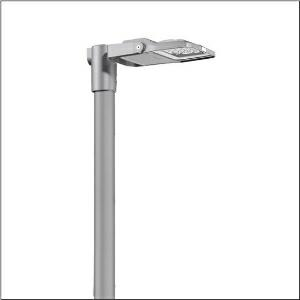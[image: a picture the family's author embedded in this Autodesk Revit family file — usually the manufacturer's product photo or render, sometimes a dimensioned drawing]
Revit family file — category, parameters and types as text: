
# Revit family: floodlight_fl_21_micro___pl33t_5xa7761a2f3a_8016
name_source: partatom
category: Lighting Fixtures
units: mm (PartAtom-declared; Revit-internal decimal feet)

## family parameters
Cut with Voids When Loaded = No
Host = Face
Light Source = No
Part Type = Normal
Room Calculation Point = No
Round Connector Dimension = Use Diameter
Shared = No

## types (1)
- --- (1 x LED, 2930 lm, 23.1 W, 3000K)
    Apparent Load = 23 VA
    CIE Flux Codes = 26 75 99 100 100
    Color Rendering = 70
    Color Temperature = 3000K
    Default Elevation = 1800 mm
    Description = Floodlight FL 21 micro, floodlight, primary light control with lens, of PMMA, primary optical cover: protective disc, of toughened safety glass, transparent, light distribution: PL33T, light emission: direct distribution, installation type: surface-mounted, LED, High Power LED, rated luminous flux: 2.930lm, luminous efficacy: 127lm/W, light colour: 730, colour temperature: 3000K, control gear: ECG iQ, control: optimised constant luminous flux control (CLO 2.0), Desk-Remote (wireless, voltage-free reading and setting of iQ features in the workshop via application-optimized NFC function/RFID function), Light-Fading, Smart-Wire, Night-Set, Lumen-Switch, Temp-Guard, Auto-Match, with terminal, 6-pole, mains connection: 220..240V, AC, 50/60Hz, start of lifetime: 23W, end of lifetime: 24W, reduction: 11W, luminaire housing, of diecast aluminium, powder-coated, Siteco® metallic grey (DB 702S), corrosivity category C5 according to DIN EN ISO 12944, mast bracket, of steel, galvanised, powder-coated, Siteco® metallic grey (DB 702S), protection rating (complete): IP66, insulation class (complete): insulation class II (safety insulation), certification: CE, protection symbol: D, impact resistance: IK07, permissible operating ambient temperature: -40..+40°C, permissible operating ambient temperature for outdoor applications: -40..+50°C, standard: DIN EN 12944, packaging unit: 1 piece

Light Distribution: PL33T
    Height = 65 mm
    Lamp = 1 x LED
    Lamp Light Flux = 2930 lm
    Lamp Power = 23.1 W
    Lamp count = 1
    Length = 312 mm
    Luminous efficacy = 127 lm/W
    Manufacturer = Siteco
    ModVariant = No
    Model = 5XA7761A2F3A
    Number of Poles = 1
    OnlyDefault = Yes
    Power Factor = 1
    Product Name = Floodlight FL 21 micro | PL33T
    Product group = floodlight | pylon top
    ProductGroupID = 6101
    Protection Class = Protection class II
    Protection Degree = IP 66
    RLX_Detail_Level = 1
    RlxData = <blob elided: 101533 chars, md5=388bebdf>
    Socket = socket
    Standby Power = 0 W
    System Light Flux = 2930 lm
    System Power = 23 W
    Type Comments = factory setting: luminous flux: 100 % | dim-lin: 254 | 455 mA
    Type Image = l_1007121.jpg
    URL = http://relux.com
    VarID = @adj_058315
    Voltage = 0 V
    Weight = 0.00 kg
    Width = 230 mm

## geometry (parser evidence)
native form markers: Blend x4, Sweep x13
no freeform markers — native parametric forms only
